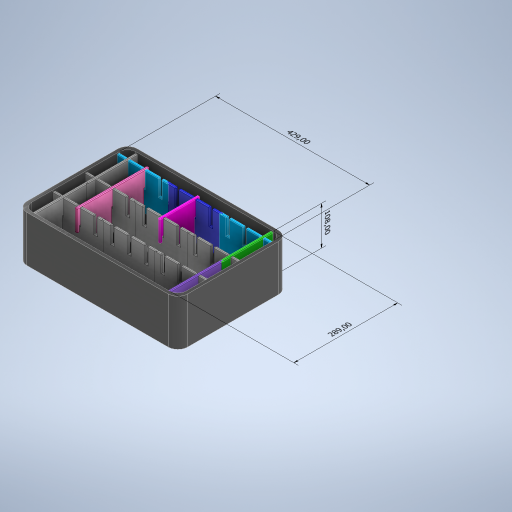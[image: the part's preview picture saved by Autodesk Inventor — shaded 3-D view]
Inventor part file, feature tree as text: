
AUTODESK INVENTOR PART (.ipt)
format: ipt  version: 2023 (Build 270158030, 158C)  size: 2,178,048 bytes
history: native  units: mm
features: other x21, extrude x21, sketch x21, fillet x20, pattern_linear x2, mirror x2
ambient origin geometry x8: Origin, YZ Plane, XZ Plane, XY Plane, X Axis, Y Axis, Z Axis, Center Point
bodies: Solid13 (feature_tree), Solid16 (feature_tree), Solid19 (feature_tree), Solid15 (feature_tree), Solid18 (feature_tree), Solid14 (feature_tree), Solid17 (feature_tree), Solid20 (feature_tree), Solid21 (feature_tree)
feature tree (87):
  other  "Flightcase Interior"
  other  "Annotations"
  extrude  "Extrusion1"  Depth=289.0mm
  extrude  "Extrusion2"  Depth=214.5mm
  fillet  "Fillet1"  Radius=9.0mm
  extrude  "Extrusion10"  Depth=9.0mm
  extrude  "Extrusion11"  Depth=23.0mm
  extrude  "Extrusion14"  Depth=108.0mm TaperAngle=0.0deg
  extrude  "Extrusion12"  Depth=20.0mm TaperAngle=0.0deg
  extrude  "Extrusion13"  Depth=15.0mm
  pattern_linear  "Rectangular Pattern1"  Spacing1=5.0mm  [1 undecoded]
  fillet  "Fillet15"  Radius=10.0mm
  fillet  "Fillet2"  Radius=15.0mm
  fillet  "Fillet3"  Radius=10.0mm
  fillet  "Fillet16"  Radius=60.0mm
  fillet  "Fillet4"  Radius=2.0mm
  fillet  "Fillet5"  Radius=2.0mm
  fillet  "Fillet6"  Radius=2.0mm
  fillet  "Fillet7"  Radius=1.5mm
  mirror  "Mirror3"
  extrude  "Extrusion15"  Depth=15.0mm
  extrude  "Extrusion16"  Depth=15.0mm
  extrude  "Extrusion17"  Depth=15.0mm TaperAngle=0.0deg
  extrude  "Extrusion18"  Depth=15.0mm
  extrude  "Extrusion19"  Depth=15.0mm TaperAngle=0.0deg
  extrude  "Extrusion20"  Depth=15.0mm
  fillet  "Fillet8"  Radius=2.0mm
  extrude  "Extrusion21"  Depth=15.0mm
  fillet  "Fillet9"  Radius=1.5mm
  extrude  "Extrusion22"  Depth=15.0mm
  fillet  "Fillet10"  Radius=61.0mm
  fillet  "Fillet11"  Radius=15.0mm
  fillet  "Fillet12"  Radius=10.0mm
  fillet  "Fillet13"  Radius=15.0mm
  fillet  "Fillet14"  Radius=10.0mm
  fillet  "Fillet17"  Radius=15.0mm
  fillet  "Fillet18"  Radius=2.0mm
  pattern_linear  "Rectangular Pattern2"  Spacing1=15.0mm  [1 undecoded]
  mirror  "Mirror4"
  extrude  "Extrusion23"  Depth=15.0mm TaperAngle=0.0deg
  extrude  "Extrusion24"  Depth=15.0mm
  extrude  "Extrusion25"  Depth=15.0mm
  extrude  "Extrusion26"  Depth=15.0mm
  extrude  "Extrusion27"  Depth=15.0mm
  extrude  "Extrusion28"  Depth=15.0mm TaperAngle=0.0deg
  fillet  "Fillet19"  Radius=7.0mm
  fillet  "Fillet20"  Radius=2.0mm
  sketch  "Sketch1"  dims[d0=429.0mm d1=289.0mm]
  sketch  "Sketch2"  dims[d2=144.5mm d3=214.5mm d4=9.0mm]
  sketch  "Sketch10"  dims[d5=9.0mm d6=9.0mm]
  other  "PART_A_hoz"
  sketch  "Sketch11"  dims[d7=9.0mm d8=23.0mm]
  sketch  "Sketch13"  dims[d9=27.0mm d10=108.0mm d11=0.0mm]
  sketch  "Sketch14"  dims[d21=27.0mm d23=20.0mm d24=0.0mm]
  other  "PART_B_hoz"
  sketch  "Sketch15"  dims[d25=15.0mm d38=7.0mm]
  sketch  "Sketch16"  dims[d120=143.0mm d125=15.0mm]
  other  "PART_C_vert"
  sketch  "Sketch17"  dims[d172=7.0mm]
  sketch  "Sketch18"  dims[d173=2.0mm]
  sketch  "Sketch19"  dims[d174=143.0mm d175=0.0mm]
  other  "PART_D_vert"
  sketch  "Sketch21"  dims[d176=7.0mm]
  sketch  "Sketch22"  dims[d177=45.0mm d178=0.0mm]
  other  "Pattern of PART_A_hoz:3"
  sketch  "Sketch24"  dims[d179=1.5mm]
  sketch  "Sketch25"  dims[d181=2.0mm]
  other  "Pattern of Solid13:4"
  other  "Pattern of Solid13:5"
  other  "Pattern of PART_B_hoz:6"
  other  "Pattern of PART_B_hoz:7"
  other  "Pattern of PART_A_hoz:8"
  other  "Pattern of PART_A_hoz:9"
  other  "Pattern of PART_C_vert:10"
  other  "Pattern of PART_D_vert:11"
  sketch  "Sketch26"  dims[d182=1.5mm]
  other  "PART_F_2waydiv"
  sketch  "Sketch28"  dims[d183=2.0mm]
  sketch  "Sketch29"  dims[d184=5.0mm]
  sketch  "Sketch30"  dims[d185=45.0mm d186=0.0mm]
  other  "PART_E_div"
  sketch  "Sketch31"  dims[d187=143.0mm]
  sketch  "Sketch32"  dims[d188=143.0mm d190=5.0mm d191=10.0mm d192=0.0mm d193=15.0mm d194=10.0mm d195=0.0mm d196=60.0mm d198=47.0mm d199=2.0mm d200=2.0mm d201=2.0mm d202=1.5mm d203=1.5mm d204=1.5mm d205=144.5mm d206=0.0mm d207=15.0mm d208=144.5mm d209=0.0mm d210=2.0mm d211=2.0mm d212=1.5mm d213=1.5mm d214=5.0mm d215=61.0mm d216=0.0mm d217=15.0mm d218=10.0mm d219=0.0mm d220=15.0mm d221=10.0mm d222=0.0mm d223=15.0mm d224=0.0mm d225=2.0mm d226=15.0mm d227=10.0mm d228=0.0mm d229=2.0mm d231=7.0mm d232=7.0mm d235=90.0mm d236=90.0mm d238=10.0mm d239=0.0mm d240=7.0mm d241=2.0mm d244=90.0mm d245=7.0mm d246=2.0mm d247=2.0mm d248=7.0mm d249=2.0mm d250=1.5mm d251=1.5mm d252=30.0mm d254=90.0mm d255=7.0mm d256=7.0mm d259=10.0mm d260=0.0mm d261=10.0mm d262=0.0mm d263=15.0mm d264=0.0mm d265=7.0mm d266=7.0mm d267=7.0mm d268=15.0mm d269=0.0mm d270=10.0mm d271=0.0mm d272=10.0mm d273=0.0mm d274=2.0mm d275=2.0mm d26=2.832357mm d27=8.593144mm d28=429.0mm d29=2.489469mm d30=6.513538mm d31=289.0mm d32=108.0mm]
  other  "General Note 1"
  other  "Linear Dimension 1"
  other  "Linear Dimension 2"
  other  "Linear Dimension 3"
note: 2 required parameter values undecoded (feature->parameter linkage not recoverable at this tier; creation-order binding heuristic only, values carry confidence <= 0.55)
